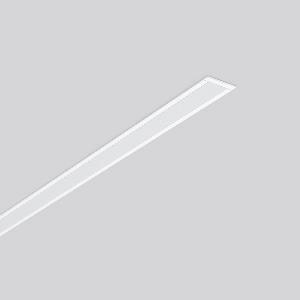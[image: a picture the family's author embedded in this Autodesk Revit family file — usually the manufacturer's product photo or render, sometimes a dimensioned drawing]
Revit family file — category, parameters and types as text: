
# Revit family: less_is_more_27_312178_002_1_6a55
name_source: partatom
category: Lighting Fixtures
units: mm (PartAtom-declared; Revit-internal decimal feet)

## family parameters
Cut with Voids When Loaded = No
Host = Face
Light Source = No
Part Type = Normal
Room Calculation Point = No
Round Connector Dimension = Use Diameter
Shared = No

## types (1)
- LESS IS MORE 27 (1 x LED Modul 840, 2900 lm, 4000)
    Apparent Load = 39 VA
    CIE Flux Codes = 48 79 96 100 100
    Color Rendering = 80
    Color Temperature = 4000
    Default Elevation = 1800 mm
    Description = Series: LESS IS MORE 27
Recessed ceiling and wall luminaire with slim design. Housing: extruded aluminium profile, powder-coated. End cap aluminium powder-coated. Diffuser made of non-yellowing plastic (PMMA), opal. Suitable for Recessed ceiling mounting, wall (recessed). External driver with connecting cable. 
Colour: traffic white, matt (RAL 9016)
Length: 1514 mm
Width: 38 mm
Height: 2 mm
Cut-out length: 1506 mm
Cut-out width: 30 mm
Recess height: 45-60 mm
Luminaire: recess height: 37 mm
Lamp: LED
Socket: without socket
Colour temperature: 4000K
Colour rendering index (CRI): 82
System power: 39 W
Rated luminous flux: 2900 lm
Luminous efficiency: 74 lm/W
Control gear: Regulated power supply
Protection class: II
Type of protection: IP 20
    Height = 0 mm  [stored 0 ft]
    Lamp = 1 x LED Modul 840
    Lamp Light Flux = 2900 lm
    Lamp count = 1
    Length = 1514 mm
    Lifetime = 50000 h
    Luminous efficacy = 74 lm/W
    Manufacturer = RZB
    ModVariant = No
    Model = 312178.002.1
    Mounting Place = Ceiling, Wall
    Mounting Type = Recessed
    Number of Poles = 1
    OnlyDefault = Yes
    Power Factor = 1
    Product Name = LESS IS MORE 27
    Product group = Recessed LED linear luminaires
    ProductGroupID = 407
    Protection Class = Protection class II
    Protection Degree = IP 20
    RLX_Detail_Level = 1
    RLX_Emergency_Light_Flux = 0 lm
    RLX_Emergency_Type = 0
    RLX_Emergency_Type_DB = No
    RlxData = <blob elided: 21553 chars, md5=2af429cc>
    Socket = socket
    Standby Power = 0 W
    System Light Flux = 2900 lm
    System Power = 39 W
    Type Comments = Product without accessories
    Type Image = 312176.002.jpg
    URL = http://relux.com
    VarID = ---
    Voltage = 230 V
    Voltage Range = 220-240 V
    Weight = 0.00 kg
    Width = 38 mm

note: [stored X ft] marks values corroborated as IEEE doubles in the binary element streams (Revit-internal decimal feet)

## geometry (parser evidence)
native form markers: Blend x4, Sweep x11
no freeform markers — native parametric forms only
